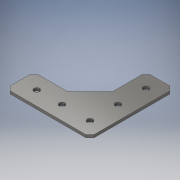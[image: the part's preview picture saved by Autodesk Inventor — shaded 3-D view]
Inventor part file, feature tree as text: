
AUTODESK INVENTOR PART (.ipt)
format: ipt  version: 2017 (Build 210142000, 142)  size: 117,248 bytes
history: native  units: in
note: dims shown in document units (in); Inventor stores cm internally (conversion verified against a paired STEP export)
features: extrude x1, sketch x1
ambient origin geometry x8: Origin, YZ Plane, XZ Plane, XY Plane, X Axis, Y Axis, Z Axis, Center Point
bodies: Body1 (feature_tree)
feature tree (2):
  extrude  "Extrusion3"  Depth=0.1in
  sketch  "Sketch1"  dims[d28=2.7in d32=0.212in d33=0.7in d34=0.212in d37=0.1in d38=0.0in]
